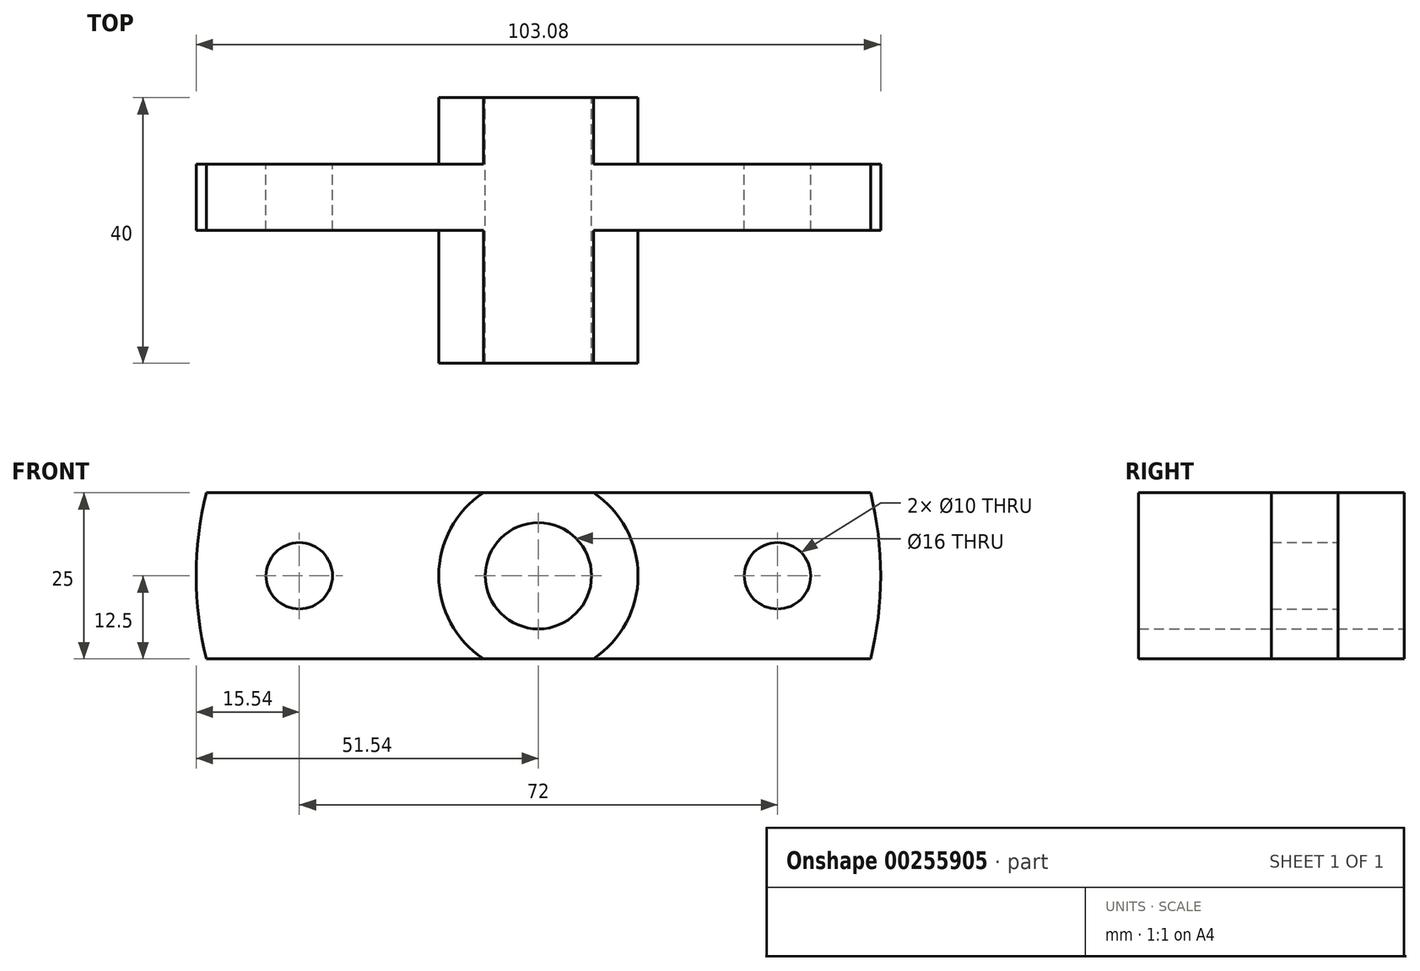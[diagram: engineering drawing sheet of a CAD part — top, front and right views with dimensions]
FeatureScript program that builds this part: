
annotation { "Feature Type Name" : "Feature", "Feature Type Description" : "" }
export const myFeature = defineFeature(function(context is Context, id is Id, definition is map)
    precondition{}
    {
        {
            var Q0;
            Q0=qCreatedBy(makeId("Front.planeOp"),FACE);
            var sketch = newSketch(context, id + "F0", { "sketchPlane" : qUnion([Q0])});
            skArc(sketch, "E0", {"start": v(0, -8) * mm, "mid": v(8, 0) * mm, "end": v(0, 8) * mm});
            skLineSegment(sketch, "E1", {"start": v(0, 12.5) * mm, "end": v(50, 12.5) * mm});
            skLineSegment(sketch, "E2", {"start": v(0, -12.5) * mm, "end": v(50, -12.5) * mm});
            skCircle(sketch, "E3", {"center": v(36, 0) * mm, "radius": 5 * mm});
            skArc(sketch, "E4.trimOffspring", {"start": v(8.3, -12.5) * mm, "mid": v(15, 0) * mm, "end": v(8.3, 12.5) * mm});
            skArc(sketch, "E5.trimOffspring", {"start": v(50, -12.5) * mm, "mid": v(51.54, 0) * mm, "end": v(50, 12.5) * mm});
            skPoint(sketch, "E6", {"position": v(0, 12.5) * mm});
            skPoint(sketch, "E7", {"position": v(0, -12.5) * mm});
            skPoint(sketch, "E8", {"position": v(0, 8) * mm});
            skPoint(sketch, "E9", {"position": v(0, -8) * mm});
            skLineSegment(sketch, "E10", {"start": v(0, 12.5) * mm, "end": v(0, -12.5) * mm});
            skSolve(sketch);
        }
        {
            var Q0;
            {var subQ4=sQuery(id+"F0.wireOp",EDGE,"E0");Q0=makeQuery(id+"F0.imprint","IMPRINT",FACE,{"disambiguationData":[TD([[makeQuery(id+"F0.imprint","IMPRINT",EDGE,{"derivedFrom":subQ4}),-1.0]])]});}
            extrude(context, id + "F1", {"entities" : qUnion([Q0]), "depth" : 30 * mm, "hasSecondDirection" : true, "secondDirectionOppositeDirection" : true, "secondDirectionDepth" : 10 * mm});
        }
        {
            var Q0;
            Q0=makeQuery(id+"F0.imprint","IMPRINT",FACE,{"disambiguationData":[TD([[makeQuery(id+"F0.imprint","IMPRINT",EDGE,{"derivedFrom":sQuery(id+"F0.wireOp",EDGE,"E3")}),-1.0]])]});
            extrude(context, id + "F2", {"entities" : qUnion([Q0]), "operationType" : NewBodyOperationType.ADD, "depth" : 10 * mm});
        }
        {
            var Q0;
            Q0=makeQuery(id+"F1.opExtrude","SWEPT_BODY",BODY,{"disambiguationData":[OSD([sQuery(id+"F0.wireOp",EDGE,"E0"),sQuery(id+"F0.wireOp",EDGE,"E1"),sQuery(id+"F0.wireOp",EDGE,"E2"),sQuery(id+"F0.wireOp",EDGE,"E4.trimOffspring"),sQuery(id+"F0.wireOp",EDGE,"E10")])]});
            var Q1;
            Q1=qCreatedBy(makeId("Right.planeOp"),FACE);
            mirror(context, id + "F3", {"operationType" : NewBodyOperationType.ADD, "entities" : qUnion([Q0]), "mirrorPlane" : qUnion([Q1])});
        }
    });
